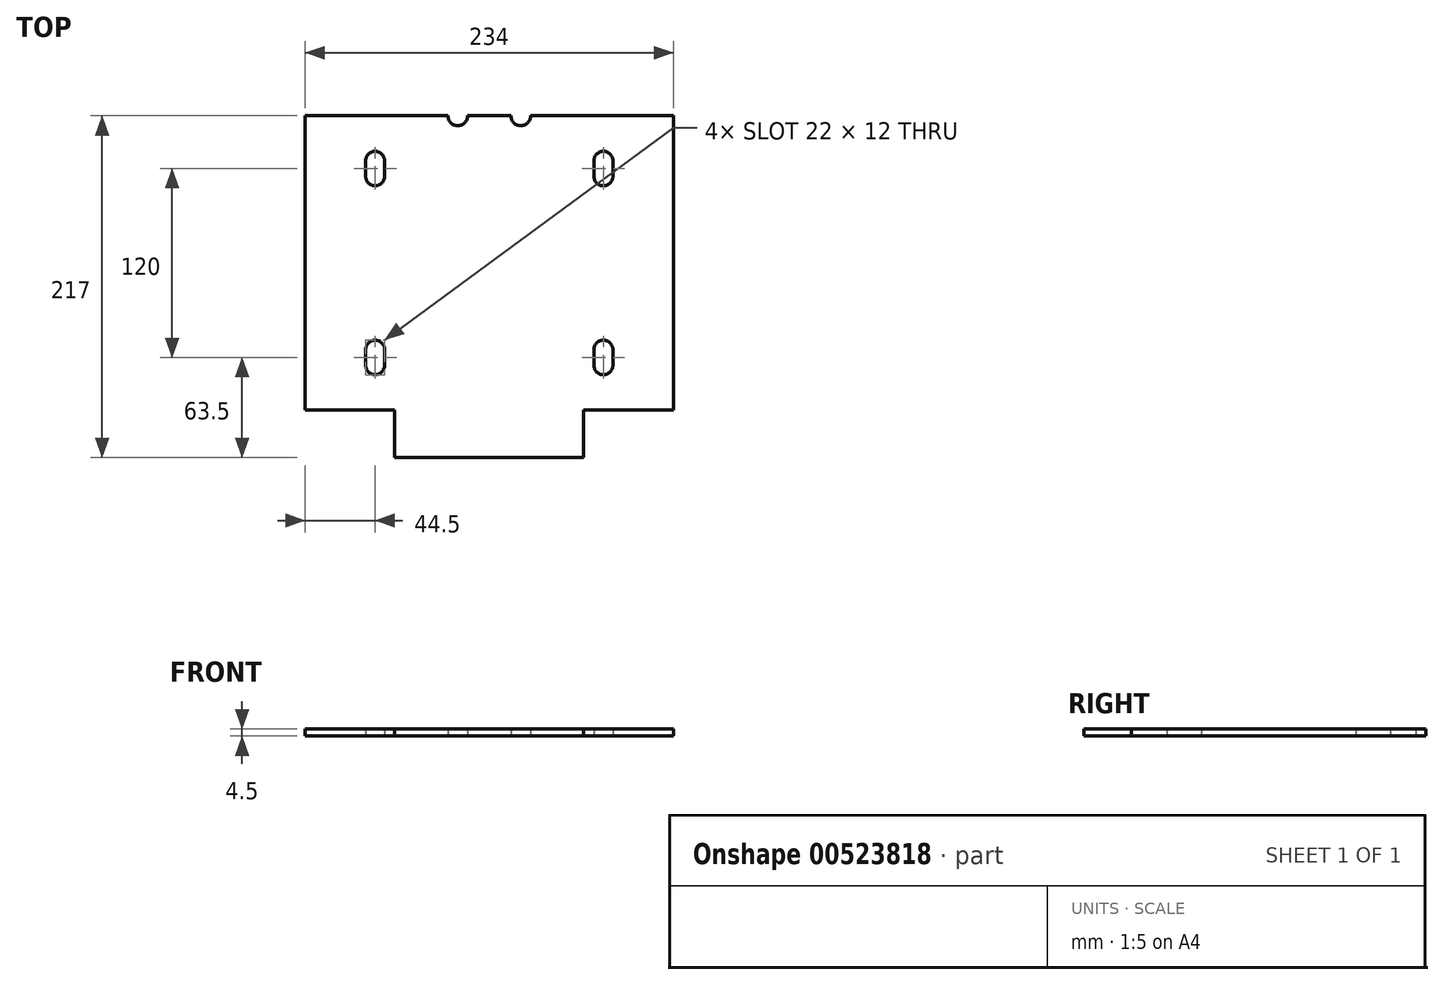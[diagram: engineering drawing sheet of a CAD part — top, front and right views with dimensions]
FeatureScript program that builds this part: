
annotation { "Feature Type Name" : "Feature", "Feature Type Description" : "" }
export const myFeature = defineFeature(function(context is Context, id is Id, definition is map)
    precondition{}
    {
        {
            var Q0;
            Q0=qCreatedBy(makeId("Top.planeOp"),FACE);
            var sketch = newSketch(context, id + "F0", { "sketchPlane" : qUnion([Q0])});
            skLineSegment(sketch, "E0.left", {"start": v(0, 0) * mm, "end": v(0, 187) * mm});
            skLineSegment(sketch, "E0.right", {"start": v(234, 0) * mm, "end": v(234, 187) * mm});
            skLineSegment(sketch, "E1", {"start": v(57, 0) * mm, "end": v(57, -30) * mm});
            skLineSegment(sketch, "E2", {"start": v(57, -30) * mm, "end": v(177, -30) * mm});
            skLineSegment(sketch, "E3", {"start": v(177, -30) * mm, "end": v(177, 0) * mm});
            skLineSegment(sketch, "E4", {"start": v(0, 0) * mm, "end": v(57, 0) * mm});
            skLineSegment(sketch, "E5", {"start": v(177, 0) * mm, "end": v(234, 0) * mm});
            skCircle(sketch, "E6", {"center": v(44.5, 148.5) * mm, "radius": 6 * mm});
            skCircle(sketch, "E7", {"center": v(189.5, 148.5) * mm, "radius": 6 * mm});
            skCircle(sketch, "E8", {"center": v(44.5, 28.5) * mm, "radius": 6 * mm});
            skCircle(sketch, "E9", {"center": v(189.5, 28.5) * mm, "radius": 6 * mm});
            skLineSegment(sketch, "E10", {"start": v(0, 187) * mm, "end": v(117, 93.5) * mm, "construction": true});
            skLineSegment(sketch, "E11", {"start": v(117, 93.5) * mm, "end": v(234, 0) * mm, "construction": true});
            skLineSegment(sketch, "E12", {"start": v(0, 187) * mm, "end": v(234, 187) * mm});
            skCircle(sketch, "E13", {"center": v(97, 187) * mm, "radius": 6.26 * mm});
            skCircle(sketch, "E14", {"center": v(137, 187) * mm, "radius": 6.26 * mm});
            skLineSegment(sketch, "E15", {"start": v(117, 187) * mm, "end": v(117, -30) * mm, "construction": true});
            skCircle(sketch, "E16.0.1.0", {"center": v(44.5, 158.5) * mm, "radius": 6 * mm});
            skCircle(sketch, "E16.0.1.1", {"center": v(189.5, 158.5) * mm, "radius": 6 * mm});
            skCircle(sketch, "E16.0.1.2", {"center": v(44.5, 38.5) * mm, "radius": 6 * mm});
            skCircle(sketch, "E16.0.1.3", {"center": v(189.5, 38.5) * mm, "radius": 6 * mm});
            skLineSegment(sketch, "E16.direction1", {"start": v(44.5, 148.5) * mm, "end": v(69.5, 148.5) * mm, "construction": true});
            skLineSegment(sketch, "E16.direction2", {"start": v(44.5, 148.5) * mm, "end": v(44.5, 158.5) * mm, "construction": true});
            skLineSegment(sketch, "E17", {"start": v(50.5, 148.5) * mm, "end": v(50.5, 158.5) * mm});
            skLineSegment(sketch, "E18", {"start": v(38.5, 148.5) * mm, "end": v(38.5, 158.5) * mm});
            skLineSegment(sketch, "E19", {"start": v(183.5, 148.5) * mm, "end": v(183.5, 158.5) * mm});
            skLineSegment(sketch, "E20", {"start": v(195.5, 158.5) * mm, "end": v(195.5, 148.5) * mm});
            skLineSegment(sketch, "E21", {"start": v(38.5, 28.5) * mm, "end": v(38.5, 38.5) * mm});
            skLineSegment(sketch, "E22", {"start": v(50.5, 28.5) * mm, "end": v(50.5, 38.5) * mm});
            skLineSegment(sketch, "E23", {"start": v(183.5, 28.5) * mm, "end": v(183.5, 38.5) * mm});
            skLineSegment(sketch, "E24", {"start": v(195.5, 28.5) * mm, "end": v(195.5, 38.5) * mm});
            skLineSegment(sketch, "E25", {"start": v(44.5, 38.5) * mm, "end": v(44.5, 28.5) * mm, "construction": true});
            skLineSegment(sketch, "E26", {"start": v(189.5, 158.5) * mm, "end": v(189.5, 148.5) * mm, "construction": true});
            skLineSegment(sketch, "E27", {"start": v(189.5, 153.5) * mm, "end": v(44.5, 33.5) * mm, "construction": true});
            skSolve(sketch);
        }
        {
            var Q0;
            Q0=makeQuery(id+"F0.imprint","IMPRINT",FACE,{"disambiguationData":[TD([[makeQuery(id+"F0.imprint","IMPRINT",EDGE,{"derivedFrom":sQuery(id+"F0.wireOp",EDGE,"E0.left")}),-1.0]])]});
            extrude(context, id + "F1", {"entities" : qUnion([Q0]), "depth" : 4.5 * mm, "offsetDistance" : 25 * mm});
        }
    });
